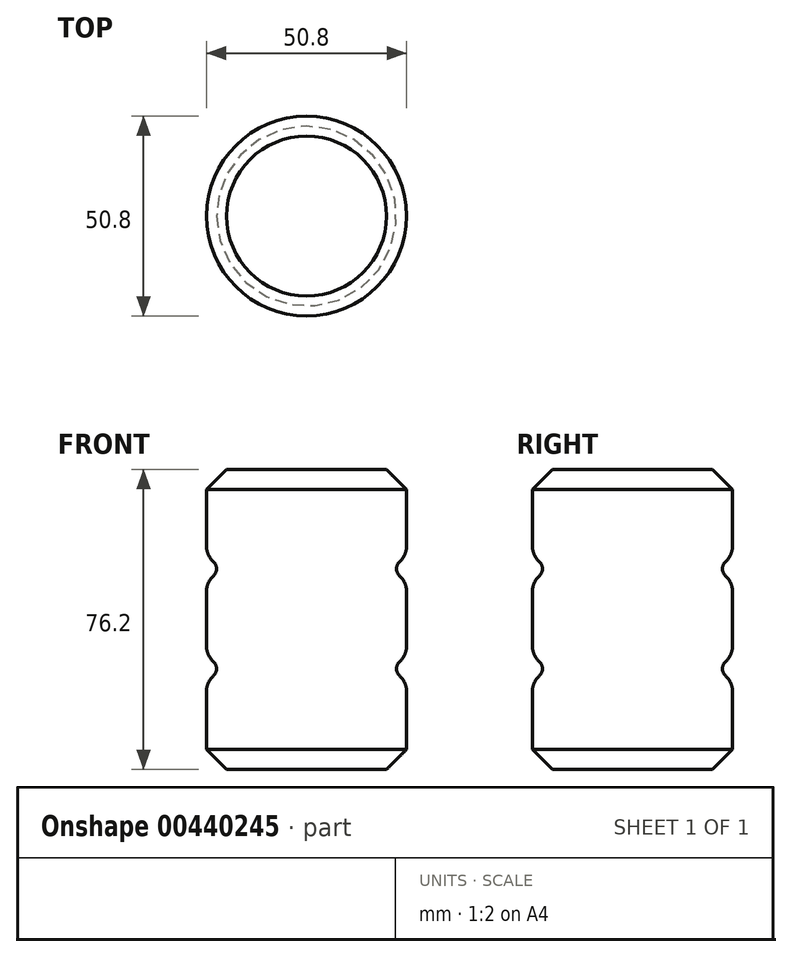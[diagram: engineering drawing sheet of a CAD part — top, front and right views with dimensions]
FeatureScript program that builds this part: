
annotation { "Feature Type Name" : "Feature", "Feature Type Description" : "" }
export const myFeature = defineFeature(function(context is Context, id is Id, definition is map)
    precondition{}
    {
        {
            var Q0;
            Q0=qCreatedBy(makeId("Front.planeOp"),FACE);
            var sketch = newSketch(context, id + "F0", { "sketchPlane" : qUnion([Q0])});
            skLineSegment(sketch, "E0.bottom", {"start": v(0, 0) * mm, "end": v(-25.4, 0) * mm});
            skLineSegment(sketch, "E0.top", {"start": v(0, 76.2) * mm, "end": v(-25.4, 76.2) * mm});
            skLineSegment(sketch, "E0.left", {"start": v(0, 0) * mm, "end": v(0, 76.2) * mm});
            skLineSegment(sketch, "E0.right", {"start": v(-25.4, 0) * mm, "end": v(-25.4, 76.2) * mm});
            skArc(sketch, "E1", {"start": v(0, 53.52) * mm, "mid": v(-2.54, 50.98) * mm, "end": v(0, 48.44) * mm});
            skArc(sketch, "E2", {"start": v(0, 28.13) * mm, "mid": v(-2.54, 25.59) * mm, "end": v(0, 23.05) * mm});
            skLineSegment(sketch, "E3", {"start": v(0, 53.52) * mm, "end": v(0, 48.44) * mm});
            skLineSegment(sketch, "E4", {"start": v(0, 28.13) * mm, "end": v(0, 23.05) * mm});
            skSolve(sketch);
        }
        {
            var Q0;
            {var subQ5=sQuery(id+"F0.wireOp",EDGE,"E0.bottom");Q0=makeQuery(id+"F0.imprint","IMPRINT",FACE,{"disambiguationData":[TD([[makeQuery(id+"F0.imprint","IMPRINT",EDGE,{"derivedFrom":subQ5}),-1.0]])]});}
            var Q1;
            Q1=sQuery(id+"F0.wireOp",EDGE,"E0.right");
            revolve(context, id + "F1", {"entities" : qUnion([Q0]), "axis" : qUnion([Q1]), "revolveType" : RevolveType.FULL});
        }
        {
            var Q0;
            Q0=makeQuery(id+"F1.opRevolve","SWEPT_FACE",FACE,{"disambiguationData":[OSD([sQuery(id+"F0.wireOp",EDGE,"E0.top")])]});
            var Q1;
            Q1=makeQuery(id+"F1.opRevolve","SWEPT_EDGE",EDGE,{"disambiguationData":[OSD([sQuery(id+"F0.wireOp",EDGE,"E0.bottom"),sQuery(id+"F0.wireOp",EDGE,"E0.left")])]});
            chamfer(context, id + "F2", {"entities" : qUnion([Q0, Q1]), "width" : 5.08 * mm, "tangentPropagation" : true});
        }
        {
            var Q0;
            {var subQ0=sQuery(id+"F0.wireOp",EDGE,"E3");var subQ1=sQuery(id+"F0.wireOp",EDGE,"E1");var subQ2=sQuery(id+"F0.wireOp",EDGE,"E0.left");Q0=makeQuery(id+"F1.opRevolve","SWEPT_EDGE",EDGE,{"disambiguationData":[OSD([subQ2,subQ1,subQ0]),TDD([makeQuery(id+"F0.imprint","INTERSECT",VERTEX,{"disambiguationData":[OD(0.0)],"derivedFrom":[subQ2,subQ1,subQ0]})])]});}
            var Q1;
            {var subQ0=sQuery(id+"F0.wireOp",EDGE,"E3");var subQ1=sQuery(id+"F0.wireOp",EDGE,"E1");var subQ2=sQuery(id+"F0.wireOp",EDGE,"E0.left");Q1=makeQuery(id+"F1.opRevolve","SWEPT_EDGE",EDGE,{"disambiguationData":[OSD([subQ2,subQ1,subQ0]),TDD([makeQuery(id+"F0.imprint","INTERSECT",VERTEX,{"disambiguationData":[OD(1.0)],"derivedFrom":[subQ2,subQ1,subQ0]})])]});}
            var Q2;
            {var subQ0=sQuery(id+"F0.wireOp",EDGE,"E4");var subQ1=sQuery(id+"F0.wireOp",EDGE,"E2");var subQ2=sQuery(id+"F0.wireOp",EDGE,"E0.left");Q2=makeQuery(id+"F1.opRevolve","SWEPT_EDGE",EDGE,{"disambiguationData":[OSD([subQ2,subQ1,subQ0]),TDD([makeQuery(id+"F0.imprint","INTERSECT",VERTEX,{"disambiguationData":[OD(0.0)],"derivedFrom":[subQ2,subQ1,subQ0]})])]});}
            var Q3;
            {var subQ0=sQuery(id+"F0.wireOp",EDGE,"E4");var subQ1=sQuery(id+"F0.wireOp",EDGE,"E2");var subQ2=sQuery(id+"F0.wireOp",EDGE,"E0.left");Q3=makeQuery(id+"F1.opRevolve","SWEPT_EDGE",EDGE,{"disambiguationData":[OSD([subQ2,subQ1,subQ0]),TDD([makeQuery(id+"F0.imprint","INTERSECT",VERTEX,{"disambiguationData":[OD(1.0)],"derivedFrom":[subQ2,subQ1,subQ0]})])]});}
            fillet(context, id + "F3", {"entities" : qUnion([Q0, Q1, Q2, Q3]), "radius" : 5.08 * mm, "tangentPropagation" : true, "allowEdgeOverflow" : false});
        }
    });
